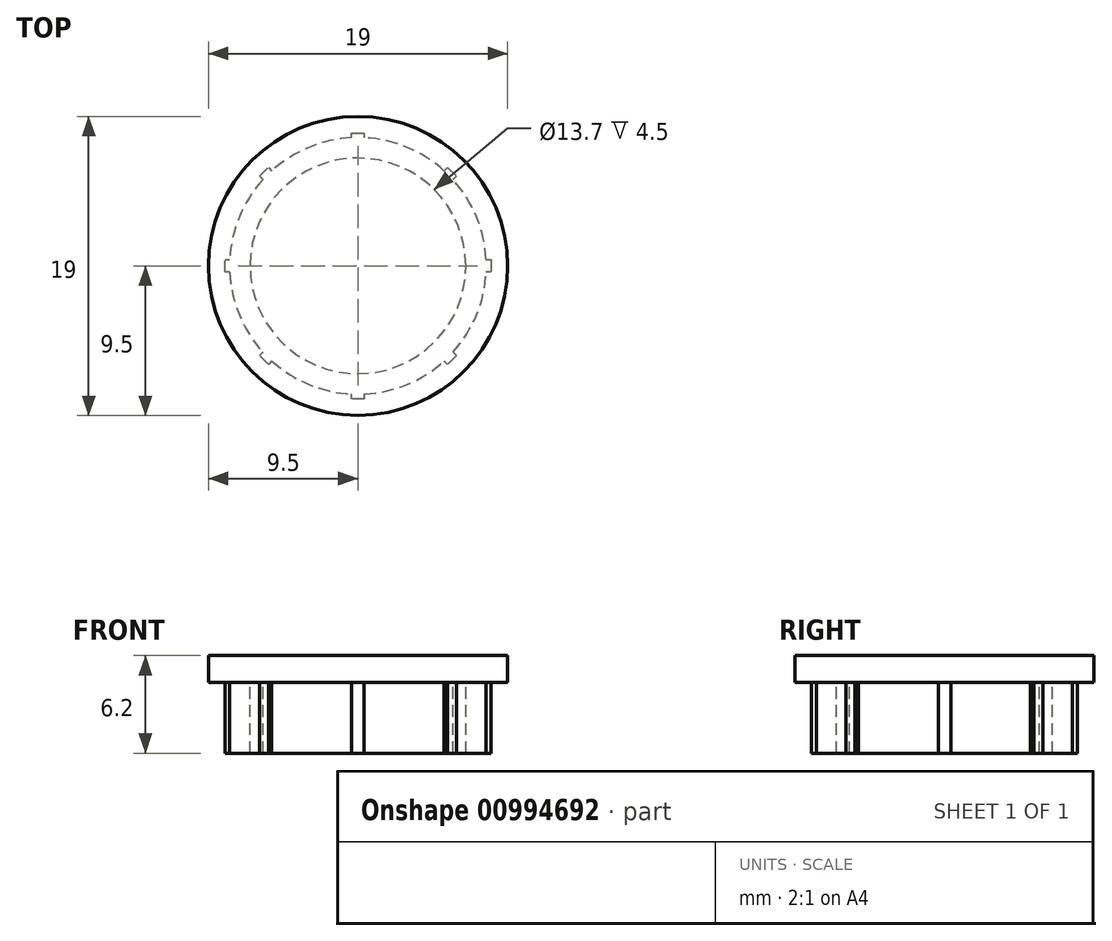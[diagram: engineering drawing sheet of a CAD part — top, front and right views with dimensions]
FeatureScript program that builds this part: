
annotation { "Feature Type Name" : "Feature", "Feature Type Description" : "" }
export const myFeature = defineFeature(function(context is Context, id is Id, definition is map)
    precondition{}
    {
        {
            var Q0;
            Q0=qCreatedBy(makeId("Top.planeOp"),FACE);
            var sketch = newSketch(context, id + "F0", { "sketchPlane" : qUnion([Q0])});
            skCircle(sketch, "E0", {"center": v(0, 0) * mm, "radius": 6.85 * mm});
            skArc(sketch, "E1", {"start": v(-0.4, 8.14) * mm, "mid": v(-3.12, 7.53) * mm, "end": v(-5.47, 6.04) * mm});
            skLineSegment(sketch, "E2", {"start": v(-0.4, 8.14) * mm, "end": v(-0.4, 8.45) * mm});
            skLineSegment(sketch, "E3", {"start": v(-0.4, 8.45) * mm, "end": v(0.4, 8.45) * mm});
            skLineSegment(sketch, "E4", {"start": v(0.4, 8.45) * mm, "end": v(0.4, 8.14) * mm});
            skLineSegment(sketch, "E5.1.0", {"start": v(-6.04, 5.47) * mm, "end": v(-6.26, 5.7) * mm});
            skLineSegment(sketch, "E5.1.1", {"start": v(-6.26, 5.7) * mm, "end": v(-5.7, 6.26) * mm});
            skLineSegment(sketch, "E5.1.2", {"start": v(-5.7, 6.26) * mm, "end": v(-5.47, 6.04) * mm});
            skLineSegment(sketch, "E5.2.0", {"start": v(-8.14, -0.4) * mm, "end": v(-8.45, -0.4) * mm});
            skLineSegment(sketch, "E5.2.1", {"start": v(-8.45, -0.4) * mm, "end": v(-8.45, 0.4) * mm});
            skLineSegment(sketch, "E5.2.2", {"start": v(-8.45, 0.4) * mm, "end": v(-8.14, 0.4) * mm});
            skLineSegment(sketch, "E5.3.0", {"start": v(-5.47, -6.04) * mm, "end": v(-5.7, -6.26) * mm});
            skLineSegment(sketch, "E5.3.1", {"start": v(-5.7, -6.26) * mm, "end": v(-6.26, -5.7) * mm});
            skLineSegment(sketch, "E5.3.2", {"start": v(-6.26, -5.7) * mm, "end": v(-6.04, -5.47) * mm});
            skLineSegment(sketch, "E5.4.0", {"start": v(0.4, -8.14) * mm, "end": v(0.4, -8.45) * mm});
            skLineSegment(sketch, "E5.4.1", {"start": v(0.4, -8.45) * mm, "end": v(-0.4, -8.45) * mm});
            skLineSegment(sketch, "E5.4.2", {"start": v(-0.4, -8.45) * mm, "end": v(-0.4, -8.14) * mm});
            skLineSegment(sketch, "E5.5.0", {"start": v(6.04, -5.47) * mm, "end": v(6.26, -5.7) * mm});
            skLineSegment(sketch, "E5.5.1", {"start": v(6.26, -5.7) * mm, "end": v(5.7, -6.26) * mm});
            skLineSegment(sketch, "E5.5.2", {"start": v(5.7, -6.26) * mm, "end": v(5.47, -6.04) * mm});
            skLineSegment(sketch, "E5.6.0", {"start": v(8.14, 0.4) * mm, "end": v(8.45, 0.4) * mm});
            skLineSegment(sketch, "E5.6.1", {"start": v(8.45, 0.4) * mm, "end": v(8.45, -0.4) * mm});
            skLineSegment(sketch, "E5.6.2", {"start": v(8.45, -0.4) * mm, "end": v(8.14, -0.4) * mm});
            skLineSegment(sketch, "E5.7.0", {"start": v(5.47, 6.04) * mm, "end": v(5.7, 6.26) * mm});
            skLineSegment(sketch, "E5.7.1", {"start": v(5.7, 6.26) * mm, "end": v(6.26, 5.7) * mm});
            skLineSegment(sketch, "E5.7.2", {"start": v(6.26, 5.7) * mm, "end": v(6.04, 5.47) * mm});
            skArc(sketch, "E6.trimOffspring", {"start": v(5.47, 6.04) * mm, "mid": v(3.12, 7.53) * mm, "end": v(0.4, 8.14) * mm});
            skArc(sketch, "E7.trimOffspring", {"start": v(-6.04, 5.47) * mm, "mid": v(-7.53, 3.12) * mm, "end": v(-8.14, 0.4) * mm});
            skArc(sketch, "E8.trimOffspring", {"start": v(-8.14, -0.4) * mm, "mid": v(-7.53, -3.12) * mm, "end": v(-6.04, -5.47) * mm});
            skArc(sketch, "E9.trimOffspring", {"start": v(-5.47, -6.04) * mm, "mid": v(-3.12, -7.53) * mm, "end": v(-0.4, -8.14) * mm});
            skArc(sketch, "E10.trimOffspring", {"start": v(0.4, -8.14) * mm, "mid": v(3.12, -7.53) * mm, "end": v(5.47, -6.04) * mm});
            skArc(sketch, "E11.trimOffspring", {"start": v(6.04, -5.47) * mm, "mid": v(7.53, -3.12) * mm, "end": v(8.14, -0.4) * mm});
            skArc(sketch, "E12.trimOffspring", {"start": v(8.14, 0.4) * mm, "mid": v(7.53, 3.12) * mm, "end": v(6.04, 5.47) * mm});
            skCircle(sketch, "E13", {"center": v(0, 0) * mm, "radius": 9.5 * mm});
            skSolve(sketch);
        }
        {
            var Q0;
            Q0=makeQuery(id+"F0.imprint","IMPRINT",FACE,{"disambiguationData":[TD([[makeQuery(id+"F0.imprint","IMPRINT",EDGE,{"derivedFrom":sQuery(id+"F0.wireOp",EDGE,"E0")}),-1.0]])]});
            extrude(context, id + "F1", {"entities" : qUnion([Q0]), "oppositeDirection" : true, "depth" : 4.5 * mm, "offsetDistance" : 25 * mm});
        }
        {
            var Q0;
            Q0=qCreatedBy(makeId("Front.planeOp"),FACE);
            var sketch = newSketch(context, id + "F2", { "sketchPlane" : qUnion([Q0])});
            skPoint(sketch, "E14", {"position": v(-9.5, 0) * mm});
            skPoint(sketch, "E15", {"position": v(0, 1.7) * mm});
            skLineSegment(sketch, "E16", {"start": v(-9.5, 0) * mm, "end": v(0, 0) * mm});
            skLineSegment(sketch, "E17", {"start": v(0, 0) * mm, "end": v(0, 1.7) * mm});
            skLineSegment(sketch, "E18", {"start": v(0, 1.7) * mm, "end": v(-9.5, 1.7) * mm});
            skLineSegment(sketch, "E19", {"start": v(-9.5, 1.7) * mm, "end": v(-9.5, 0) * mm});
            skSolve(sketch);
        }
        {
            var Q0;
            {var subQ3=sQuery(id+"F2.wireOp",EDGE,"E17");Q0=makeQuery(id+"F2.imprint","IMPRINT",FACE,{"disambiguationData":[TD([[makeQuery(id+"F2.imprint","IMPRINT",EDGE,{"derivedFrom":subQ3}),1.0]])]});}
            var Q1;
            {var subQ3=sQuery(id+"F2.wireOp",EDGE,"E17");Q1=makeQuery(id+"F2.imprint","IMPRINT",FACE,{"disambiguationData":[TD([[makeQuery(id+"F2.imprint","IMPRINT",EDGE,{"derivedFrom":subQ3}),-1.0]])]});}
            var Q2;
            Q2=sQuery(id+"F2.wireOp",EDGE,"E17");
            revolve(context, id + "F3", {"surfaceOperationType" : NewSurfaceOperationType.NEW, "entities" : qUnion([Q0, Q1]), "axis" : qUnion([Q2]), "revolveType" : RevolveType.ONE_DIRECTION, "angle" : 180 * degree});
        }
        {
            var Q0;
            Q0=makeQuery(id+"F2.imprint","IMPRINT",FACE,{"disambiguationData":[TD([[makeQuery(id+"F2.imprint","IMPRINT",EDGE,{"derivedFrom":sQuery(id+"F2.wireOp",EDGE,"Peg3V2m5-vTD3-85SU-pJHs-dHWT2mhJ38YM")}),1.0]])]});
            var Q1;
            Q1=makeQuery(id+"F2.imprint","IMPRINT",FACE,{"disambiguationData":[TD([[makeQuery(id+"F2.imprint","IMPRINT",EDGE,{"derivedFrom":sQuery(id+"F2.wireOp",EDGE,"E16")}),1.0]])]});
            var Q2;
            Q2=sQuery(id+"F2.wireOp",EDGE,"E17");
            revolve(context, id + "F4", {"surfaceOperationType" : NewSurfaceOperationType.NEW, "entities" : qUnion([Q0, Q1]), "axis" : qUnion([Q2]), "revolveType" : RevolveType.FULL});
        }
        {
            var Q0;
            Q0=makeQuery(id+"F3.opRevolve","SWEPT_BODY",BODY,{"disambiguationData":[OSD([sQuery(id+"F2.wireOp",EDGE,"Peg3V2m5-vTD3-85SU-pJHs-dHWT2mhJ38YM"),sQuery(id+"F2.wireOp",EDGE,"E16"),sQuery(id+"F2.wireOp",EDGE,"E17")])]});
            deleteBodies(context, id + "F5", {"entities" : qUnion([Q0])});
        }
    });
